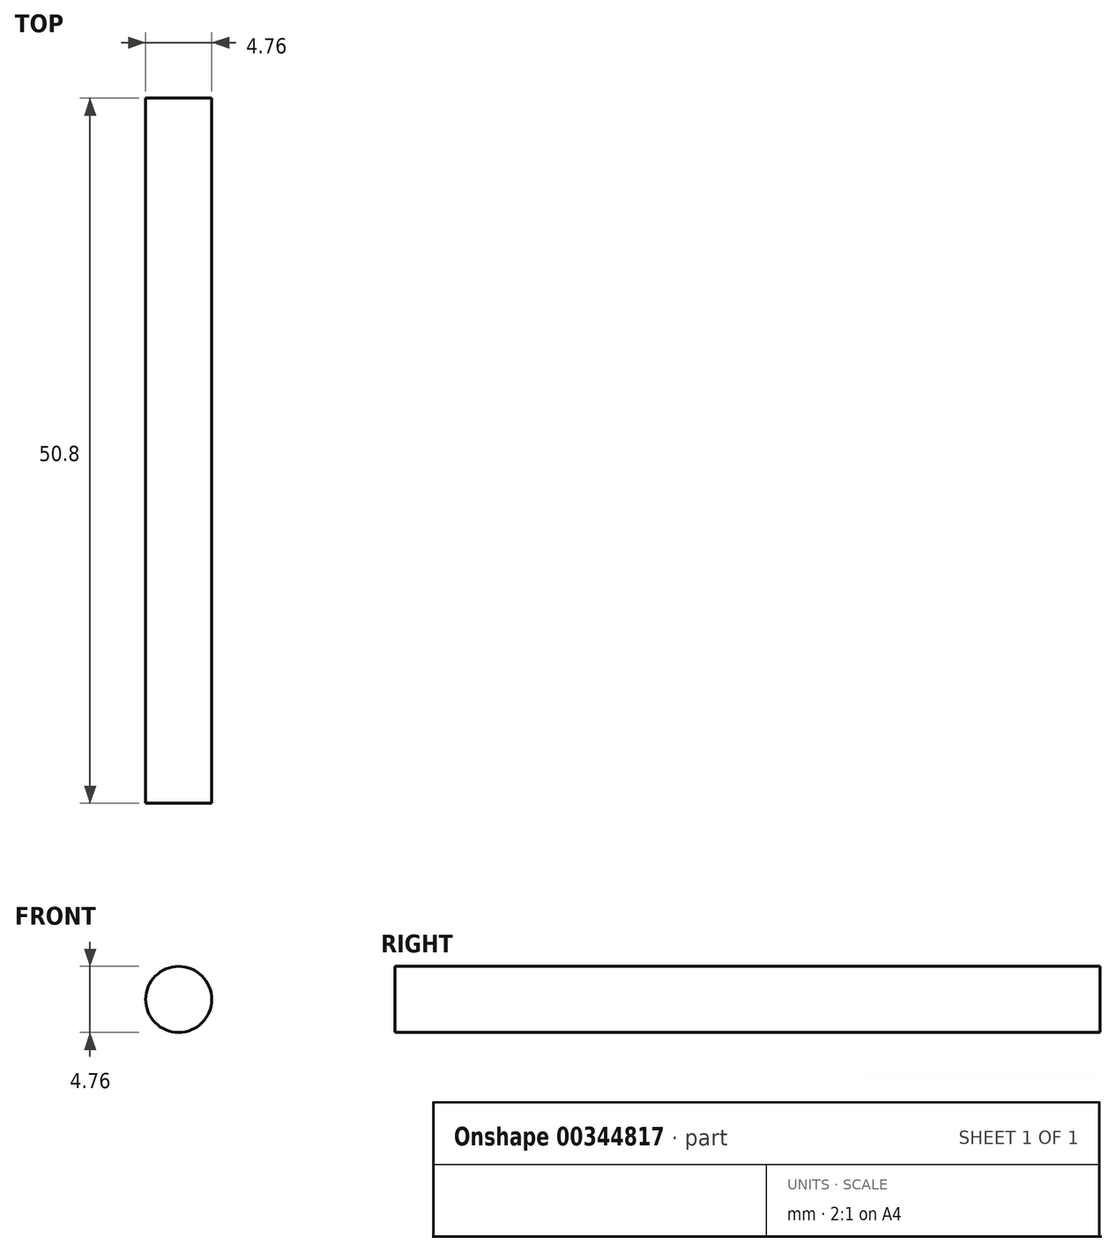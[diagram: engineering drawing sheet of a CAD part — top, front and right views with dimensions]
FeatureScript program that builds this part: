
annotation { "Feature Type Name" : "Feature", "Feature Type Description" : "" }
export const myFeature = defineFeature(function(context is Context, id is Id, definition is map)
    precondition{}
    {
        {
            var Q0;
            Q0=qCreatedBy(makeId("Front.planeOp"),FACE);
            var sketch = newSketch(context, id + "F0", { "sketchPlane" : qUnion([Q0])});
            skCircle(sketch, "E0", {"center": v(0, 0) * mm, "radius": 2.38 * mm});
            skSolve(sketch);
        }
        {
            var Q0;
            Q0=makeQuery(id+"F0.imprint","IMPRINT",FACE,{"disambiguationData":[TD([[makeQuery(id+"F0.imprint","IMPRINT",EDGE,{"derivedFrom":sQuery(id+"F0.wireOp",EDGE,"E0")}),1.0]])]});
            extrude(context, id + "F1", {"entities" : qUnion([Q0]), "depth" : 50.8 * mm});
        }
    });
